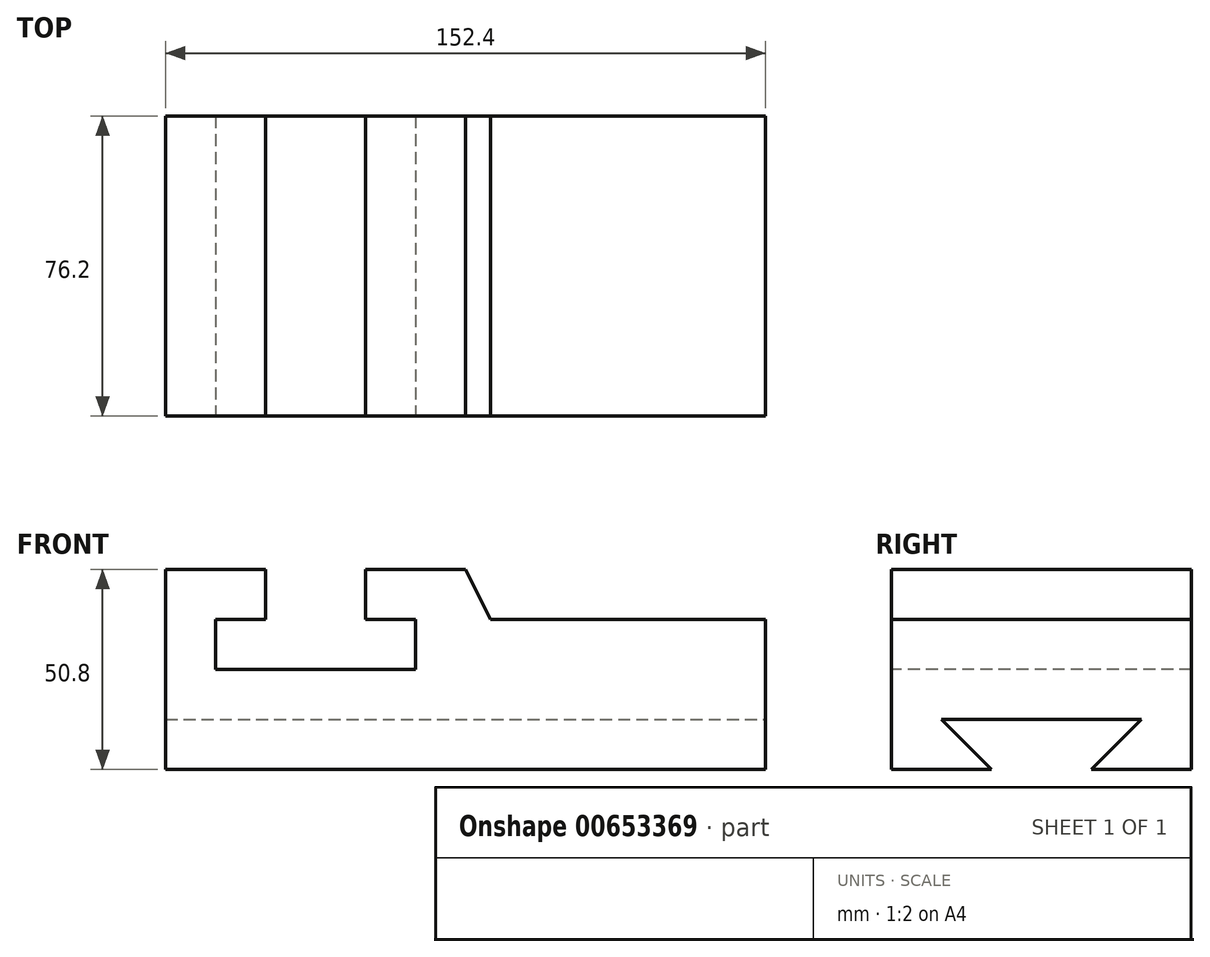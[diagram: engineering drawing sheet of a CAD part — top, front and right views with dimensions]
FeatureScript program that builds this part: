
annotation { "Feature Type Name" : "Feature", "Feature Type Description" : "" }
export const myFeature = defineFeature(function(context is Context, id is Id, definition is map)
    precondition{}
    {
        {
            var Q0;
            Q0=qCreatedBy(makeId("Front.planeOp"),FACE);
            var sketch = newSketch(context, id + "F0", { "sketchPlane" : qUnion([Q0])});
            skLineSegment(sketch, "E0", {"start": v(-76.33, 0) * mm, "end": v(76.07, 0) * mm});
            skLineSegment(sketch, "E1", {"start": v(-76.33, 0) * mm, "end": v(-76.33, 50.8) * mm});
            skLineSegment(sketch, "E2", {"start": v(-76.33, 50.8) * mm, "end": v(-50.93, 50.8) * mm});
            skLineSegment(sketch, "E3", {"start": v(-50.93, 50.8) * mm, "end": v(-50.93, 38.1) * mm});
            skLineSegment(sketch, "E4", {"start": v(-50.93, 38.1) * mm, "end": v(-63.63, 38.1) * mm});
            skPoint(sketch, "E4.endSnap0", {"position": v(-63.63, 50.8) * mm});
            skLineSegment(sketch, "E5", {"start": v(-63.63, 38.1) * mm, "end": v(-63.63, 25.4) * mm});
            skLineSegment(sketch, "E6", {"start": v(-63.63, 25.4) * mm, "end": v(-12.83, 25.4) * mm});
            skLineSegment(sketch, "E7", {"start": v(-12.83, 25.4) * mm, "end": v(-12.83, 38.1) * mm});
            skLineSegment(sketch, "E8", {"start": v(-12.83, 38.1) * mm, "end": v(-25.53, 38.1) * mm});
            skLineSegment(sketch, "E9", {"start": v(-25.53, 38.1) * mm, "end": v(-25.53, 50.8) * mm});
            skLineSegment(sketch, "E10", {"start": v(-25.53, 50.8) * mm, "end": v(-0.13, 50.8) * mm});
            skLineSegment(sketch, "E11", {"start": v(6.22, 38.1) * mm, "end": v(-0.13, 50.8) * mm});
            skLineSegment(sketch, "E12", {"start": v(6.22, 38.1) * mm, "end": v(76.07, 38.1) * mm});
            skLineSegment(sketch, "E13", {"start": v(76.07, 38.1) * mm, "end": v(76.07, 0) * mm});
            skSolve(sketch);
        }
        {
            var Q0;
            Q0=makeQuery(id+"F0.imprint","IMPRINT",FACE,{"disambiguationData":[TD([[makeQuery(id+"F0.imprint","IMPRINT",EDGE,{"derivedFrom":sQuery(id+"F0.wireOp",EDGE,"E0")}),1.0]])]});
            extrude(context, id + "F1", {"entities" : qUnion([Q0]), "oppositeDirection" : true, "depth" : 76.2 * mm, "offsetDistance" : 25.4 * mm});
        }
        {
            var Q0;
            Q0=makeQuery(id+"F1.opExtrude","SWEPT_FACE",FACE,{"disambiguationData":[OSD([sQuery(id+"F0.wireOp",EDGE,"E13")])]});
            var sketch = newSketch(context, id + "F2", { "sketchPlane" : qUnion([Q0])});
            skLineSegment(sketch, "E14", {"start": v(0, 0) * mm, "end": v(25.4, 0) * mm});
            skPoint(sketch, "E15.endSnap0", {"position": v(12.7, 0) * mm});
            skLineSegment(sketch, "E16", {"start": v(12.7, 12.7) * mm, "end": v(25.4, 0) * mm});
            skLineSegment(sketch, "E17", {"start": v(12.7, 12.7) * mm, "end": v(63.5, 12.7) * mm});
            skLineSegment(sketch, "E18", {"start": v(76.2, 0) * mm, "end": v(50.8, 0) * mm});
            skLineSegment(sketch, "E19", {"start": v(63.5, 12.7) * mm, "end": v(50.8, 0) * mm});
            skSolve(sketch);
        }
        {
            var Q0;
            {var subQ0=sQuery(id+"F2.wireOp",EDGE,"E16");Q0=makeQuery(id+"F2.imprint","IMPRINT",FACE,{"disambiguationData":[TD([[makeQuery(id+"F2.imprint","IMPRINT",EDGE,{"derivedFrom":subQ0}),1.0]])]});}
            extrude(context, id + "F3", {"entities" : qUnion([Q0]), "operationType" : NewBodyOperationType.REMOVE, "oppositeDirection" : true, "depth" : 152.4 * mm, "offsetDistance" : 25.4 * mm});
        }
    });
